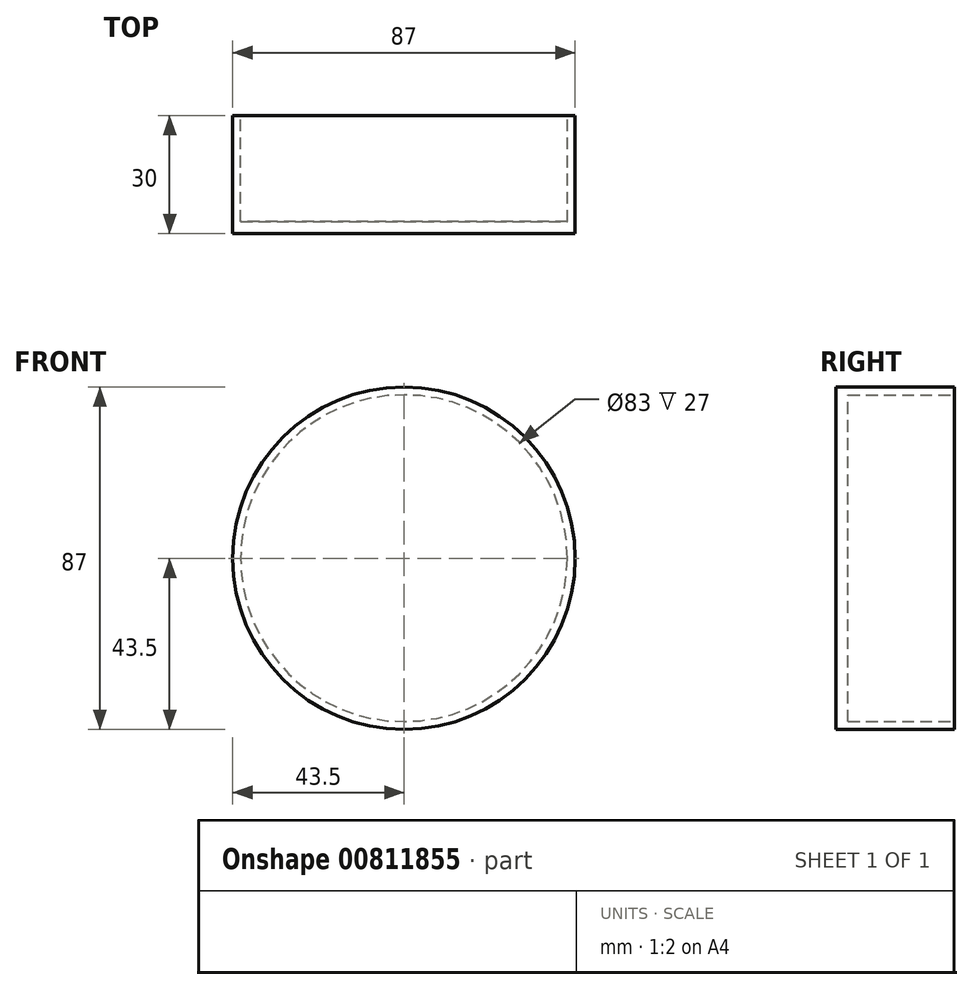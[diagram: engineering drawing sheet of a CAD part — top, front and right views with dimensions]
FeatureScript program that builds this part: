
annotation { "Feature Type Name" : "Feature", "Feature Type Description" : "" }
export const myFeature = defineFeature(function(context is Context, id is Id, definition is map)
    precondition{}
    {
        {
            var Q0;
            Q0=qCreatedBy(makeId("Front.planeOp"),FACE);
            var sketch = newSketch(context, id + "F0", { "sketchPlane" : qUnion([Q0])});
            skCircle(sketch, "E0", {"center": v(0, 0) * mm, "radius": 43.5 * mm});
            skCircle(sketch, "E1", {"center": v(0, 0) * mm, "radius": 41.5 * mm});
            skSolve(sketch);
        }
        {
            var Q0;
            Q0=makeQuery(id+"F0.imprint","IMPRINT",FACE,{"disambiguationData":[TD([[makeQuery(id+"F0.imprint","IMPRINT",EDGE,{"derivedFrom":sQuery(id+"F0.wireOp",EDGE,"E1")}),1.0]])]});
            var Q1;
            Q1=makeQuery(id+"F0.imprint","IMPRINT",FACE,{"disambiguationData":[TD([[makeQuery(id+"F0.imprint","IMPRINT",EDGE,{"derivedFrom":sQuery(id+"F0.wireOp",EDGE,"E0")}),1.0]])]});
            extrude(context, id + "F1", {"entities" : qUnion([Q0, Q1]), "depth" : 30 * mm, "offsetDistance" : 25 * mm});
        }
        {
            var Q0;
            Q0=makeQuery(id+"F0.imprint","IMPRINT",FACE,{"disambiguationData":[TD([[makeQuery(id+"F0.imprint","IMPRINT",EDGE,{"derivedFrom":sQuery(id+"F0.wireOp",EDGE,"E1")}),1.0]])]});
            extrude(context, id + "F2", {"entities" : qUnion([Q0]), "operationType" : NewBodyOperationType.REMOVE, "depth" : 27 * mm, "offsetDistance" : 25 * mm});
        }
    });
